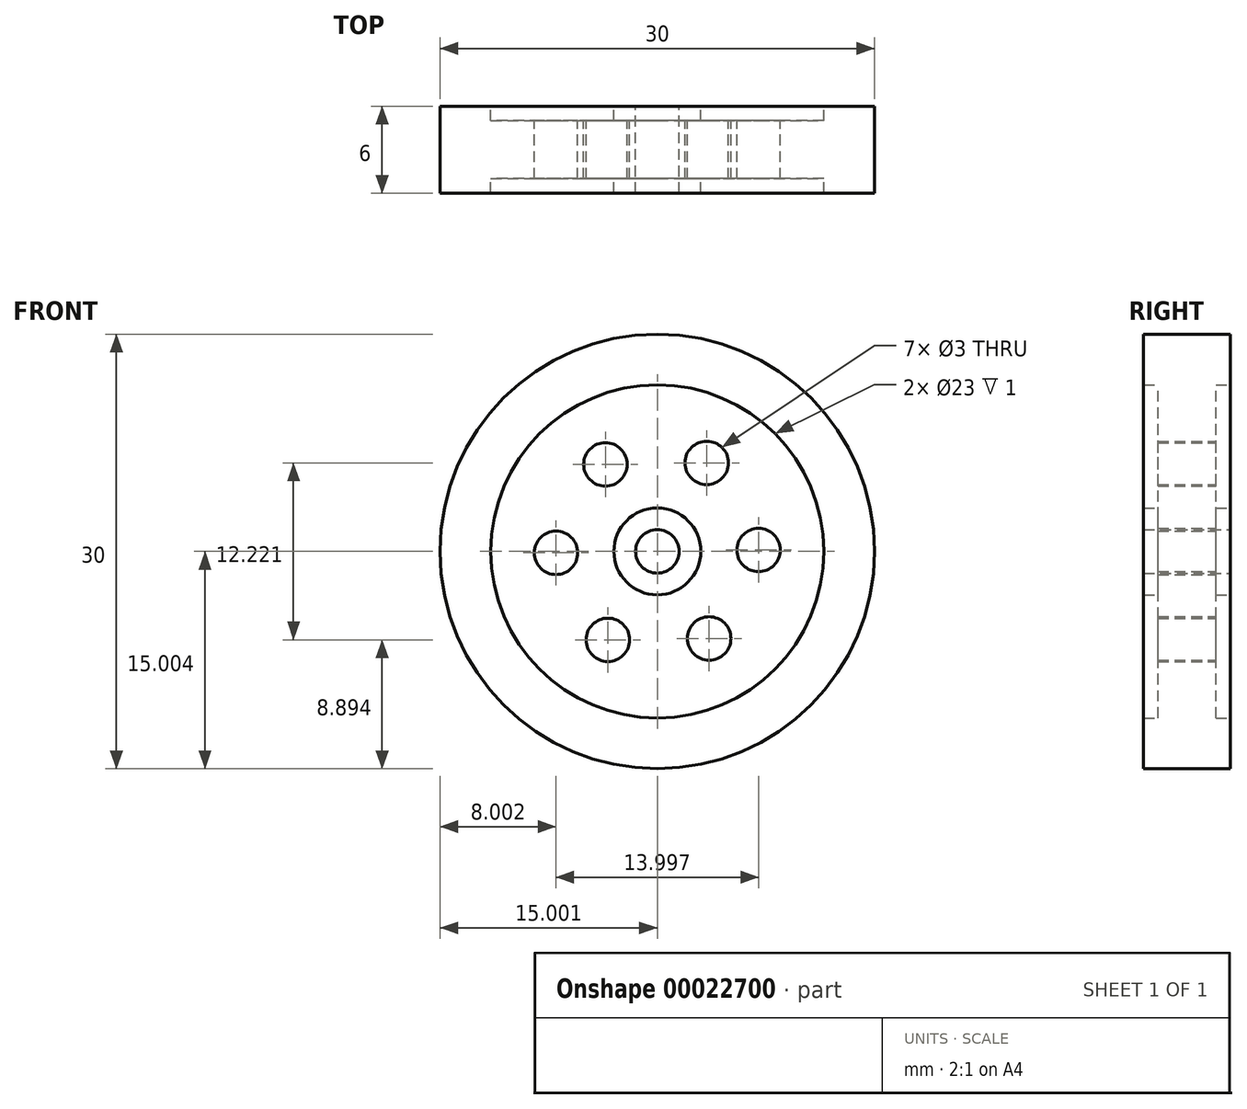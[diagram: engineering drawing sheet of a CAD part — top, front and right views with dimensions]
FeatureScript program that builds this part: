
annotation { "Feature Type Name" : "Feature", "Feature Type Description" : "" }
export const myFeature = defineFeature(function(context is Context, id is Id, definition is map)
    precondition{}
    {
        {
            var Q0;
            Q0=qCreatedBy(makeId("Front.planeOp"),FACE);
            var sketch = newSketch(context, id + "F0", { "sketchPlane" : qUnion([Q0])});
            skCircle(sketch, "E0", {"center": v(3.78, 20.5) * mm, "radius": 15 * mm});
            skCircle(sketch, "E1", {"center": v(3.78, 20.5) * mm, "radius": 11.5 * mm});
            skCircle(sketch, "E2", {"center": v(3.78, 20.5) * mm, "radius": 3 * mm});
            skCircle(sketch, "E3", {"center": v(3.78, 20.5) * mm, "radius": 1.5 * mm});
            skCircle(sketch, "E4", {"center": v(-3.22, 20.4) * mm, "radius": 1.5 * mm});
            skCircle(sketch, "E5.1.0", {"center": v(0.37, 14.4) * mm, "radius": 1.5 * mm});
            skCircle(sketch, "E5.2.0", {"center": v(7.37, 14.5) * mm, "radius": 1.5 * mm});
            skCircle(sketch, "E6.1.3.0", {"center": v(10.78, 20.6) * mm, "radius": 1.5 * mm});
            skCircle(sketch, "E6.1.4.0", {"center": v(7.2, 26.61) * mm, "radius": 1.5 * mm});
            skCircle(sketch, "E6.1.5.0", {"center": v(0.2, 26.52) * mm, "radius": 1.5 * mm});
            skLineSegment(sketch, "E7", {"start": v(-1.3, 20.4) * mm, "end": v(-1.72, 20.4) * mm});
            skSolve(sketch);
        }
        {
            var Q0;
            Q0=makeQuery(id+"F0.imprint","IMPRINT",FACE,{"disambiguationData":[TD([[makeQuery(id+"F0.imprint","IMPRINT",EDGE,{"derivedFrom":sQuery(id+"F0.wireOp",EDGE,"E0")}),1.0]])]});
            extrude(context, id + "F1", {"entities" : qUnion([Q0]), "endBound" : BoundingType.SYMMETRIC, "depth" : 6 * mm});
        }
        {
            var Q0;
            Q0=makeQuery(id+"F0.imprint","IMPRINT",FACE,{"disambiguationData":[TD([[makeQuery(id+"F0.imprint","IMPRINT",EDGE,{"derivedFrom":sQuery(id+"F0.wireOp",EDGE,"E1")}),1.0]])]});
            extrude(context, id + "F2", {"entities" : qUnion([Q0]), "operationType" : NewBodyOperationType.ADD, "endBound" : BoundingType.SYMMETRIC, "depth" : 4 * mm});
        }
        {
            var Q0;
            Q0=makeQuery(id+"F0.imprint","IMPRINT",FACE,{"disambiguationData":[TD([[makeQuery(id+"F0.imprint","IMPRINT",EDGE,{"derivedFrom":sQuery(id+"F0.wireOp",EDGE,"E2")}),1.0]])]});
            extrude(context, id + "F3", {"entities" : qUnion([Q0]), "operationType" : NewBodyOperationType.ADD, "endBound" : BoundingType.SYMMETRIC, "depth" : 6 * mm});
        }
    });
